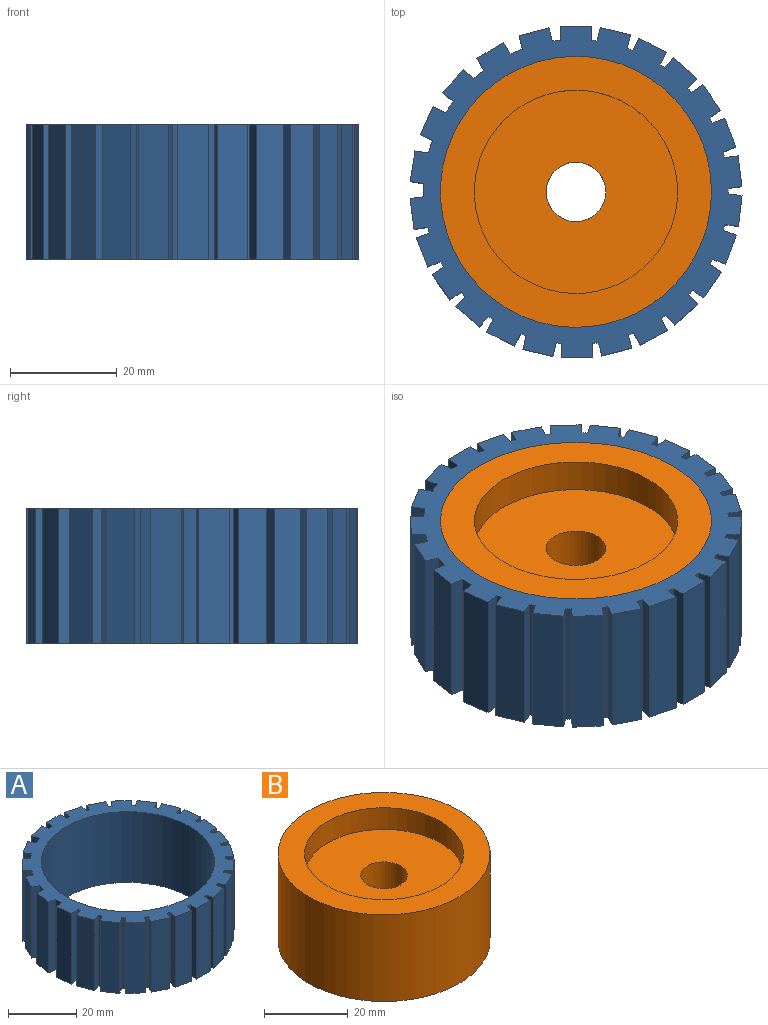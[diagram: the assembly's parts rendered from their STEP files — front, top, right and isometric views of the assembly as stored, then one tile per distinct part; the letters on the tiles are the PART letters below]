
ASSEMBLY  parts=2 mates=1
PART A: 103 faces, bbox 62.2x62x25.4 mm
  f0: plane 25.4x2.54mm, normal (0.13,-0.99,0), area 65.2mm2, adj f1,f99,f101,f102
  f1: cylinder r=28.57mm len=25.4mm, axis (0,0,-1), area 27.2mm2, adj f0,f2,f101,f102
  f2: plane 25.4x2.39mm, normal (-0.37,0.93,0), area 65.2mm2, adj f1,f3,f101,f102
  f3: plane 25.4x5.4mm, normal (-0.93,-0.37,0), area 147.4mm2, adj f2,f4,f101,f102
  f4: plane 25.4x2.39mm, normal (0.37,-0.93,0), area 65.2mm2, adj f3,f5,f101,f102
  f5: cylinder r=28.57mm len=25.4mm, axis (0,0,-1), area 27.2mm2, adj f4,f6,f101,f102
  f6: plane 25.4x2.09mm, normal (-0.58,0.82,0), area 65.2mm2, adj f5,f7,f101,f102
  f7: plane 25.4x4.74mm, normal (-0.82,-0.58,0), area 147.4mm2, adj f6,f8,f101,f102
  f8: plane 25.4x2.09mm, normal (0.58,-0.82,0), area 65.2mm2, adj f7,f9,f101,f102
  f9: cylinder r=28.57mm len=25.4mm, axis (0,0,-1), area 27.2mm2, adj f8,f10,f101,f102
  f10: plane 25.4x1.94mm, normal (-0.76,0.65,0), area 65.2mm2, adj f9,f11,f101,f102
  f11: plane 25.4x4.39mm, normal (-0.65,-0.76,0), area 147.4mm2, adj f10,f12,f101,f102
  f12: plane 25.4x1.94mm, normal (0.76,-0.65,0), area 65.2mm2, adj f11,f13,f101,f102
  f13: cylinder r=28.57mm len=25.4mm, axis (0,0,-1), area 27.2mm2, adj f12,f14,f101,f102
  f14: plane 25.4x2.28mm, normal (-0.89,0.46,0), area 65.2mm2, adj f13,f15,f101,f102
  f15: plane 25.4x5.17mm, normal (-0.46,-0.89,0), area 147.4mm2, adj f14,f16,f101,f102
  f16: plane 25.4x2.28mm, normal (0.89,-0.46,0), area 65.2mm2, adj f15,f17,f101,f102
  f17: cylinder r=28.57mm len=25.4mm, axis (0,0,-1), area 27.2mm2, adj f16,f18,f101,f102
  f18: plane 25.4x2.5mm, normal (-0.97,0.23,0), area 65.2mm2, adj f17,f19,f101,f102
  f19: plane 25.4x5.65mm, normal (-0.23,-0.97,0), area 147.4mm2, adj f18,f20,f101,f102
  f20: plane 25.4x2.5mm, normal (0.97,-0.23,0), area 65.2mm2, adj f19,f21,f101,f102
  f21: cylinder r=28.57mm len=25.4mm, axis (0,0,-1), area 27.2mm2, adj f20,f22,f101,f102
  f22: plane 25.4x2.57mm, normal (-1,-0.01,0), area 65.2mm2, adj f21,f23,f101,f102
  f23: plane 25.4x5.8mm, normal (0.01,-1,0), area 147.4mm2, adj f22,f24,f101,f102
  f24: plane 25.4x2.57mm, normal (1,0.01,0), area 65.2mm2, adj f23,f25,f101,f102
  f25: cylinder r=28.57mm len=25.4mm, axis (0,0,-1), area 27.2mm2, adj f24,f26,f101,f102
  f26: plane 25.4x2.49mm, normal (-0.97,-0.25,0), area 65.2mm2, adj f25,f27,f101,f102
  f27: plane 25.4x5.62mm, normal (0.25,-0.97,0), area 147.4mm2, adj f26,f28,f101,f102
  f28: plane 25.4x2.49mm, normal (0.97,0.25,0), area 65.2mm2, adj f27,f29,f101,f102
  f29: cylinder r=28.57mm len=25.4mm, axis (0,0,-1), area 27.2mm2, adj f28,f30,f101,f102
  f30: plane 25.4x2.26mm, normal (-0.88,-0.47,0), area 65.2mm2, adj f29,f31,f101,f102
  f31: plane 25.4x5.12mm, normal (0.47,-0.88,0), area 147.4mm2, adj f30,f32,f101,f102
  f32: plane 25.4x2.26mm, normal (0.88,0.47,0), area 65.2mm2, adj f31,f33,f101,f102
  f33: cylinder r=28.57mm len=25.4mm, axis (0,0,-1), area 27.2mm2, adj f32,f34,f101,f102
  f34: plane 25.4x1.91mm, normal (-0.74,-0.67,0), area 65.2mm2, adj f33,f35,f101,f102
  f35: plane 25.4x4.32mm, normal (0.67,-0.74,0), area 147.4mm2, adj f34,f36,f101,f102
  f36: plane 25.4x1.91mm, normal (0.74,0.67,0), area 65.2mm2, adj f35,f37,f101,f102
  f37: cylinder r=28.57mm len=25.4mm, axis (0,0,-1), area 27.2mm2, adj f36,f38,f101,f102
  f38: plane 25.4x2.12mm, normal (-0.56,-0.83,0), area 65.2mm2, adj f37,f39,f101,f102
  f39: plane 25.4x4.8mm, normal (0.83,-0.56,0), area 147.4mm2, adj f38,f40,f101,f102
  f40: plane 25.4x2.12mm, normal (0.56,0.83,0), area 65.2mm2, adj f39,f41,f101,f102
  f41: cylinder r=28.57mm len=25.4mm, axis (0,0,-1), area 27.2mm2, adj f40,f42,f101,f102
  f42: plane 25.4x2.4mm, normal (-0.35,-0.94,0), area 65.2mm2, adj f41,f43,f101,f102
  f43: plane 25.4x5.44mm, normal (0.94,-0.35,0), area 147.4mm2, adj f42,f44,f101,f102
  f44: plane 25.4x2.4mm, normal (0.35,0.94,0), area 65.2mm2, adj f43,f45,f101,f102
  f45: cylinder r=28.57mm len=25.4mm, axis (0,0,-1), area 27.2mm2, adj f44,f46,f101,f102
  f46: plane 25.4x2.55mm, normal (-0.12,-0.99,0), area 65.2mm2, adj f45,f47,f101,f102
  f47: plane 25.4x5.76mm, normal (0.99,-0.12,0), area 147.4mm2, adj f46,f48,f101,f102
  f48: plane 25.4x2.55mm, normal (0.12,0.99,0), area 65.2mm2, adj f47,f49,f101,f102
  f49: cylinder r=28.57mm len=25.4mm, axis (0,0,-1), area 27.2mm2, adj f48,f50,f101,f102
  f50: plane 25.4x2.55mm, normal (0.12,-0.99,0), area 65.2mm2, adj f49,f51,f101,f102
  f51: plane 25.4x5.76mm, normal (0.99,0.12,0), area 147.4mm2, adj f50,f52,f101,f102
  f52: plane 25.4x2.55mm, normal (-0.12,0.99,0), area 65.2mm2, adj f51,f53,f101,f102
  f53: cylinder r=28.57mm len=25.4mm, axis (0,0,-1), area 27.2mm2, adj f52,f54,f101,f102
  f54: plane 25.4x2.4mm, normal (0.36,-0.93,0), area 65.2mm2, adj f53,f55,f101,f102
  f55: plane 25.4x5.42mm, normal (0.93,0.36,0), area 147.4mm2, adj f54,f56,f101,f102
  f56: plane 25.4x2.4mm, normal (-0.36,0.93,0), area 65.2mm2, adj f55,f57,f101,f102
  f57: cylinder r=28.57mm len=25.4mm, axis (0,0,-1), area 27.2mm2, adj f56,f58,f101,f102
  f58: plane 25.4x2.11mm, normal (0.57,-0.82,0), area 65.2mm2, adj f57,f59,f101,f102
  f59: plane 25.4x4.77mm, normal (0.82,0.57,0), area 147.4mm2, adj f58,f60,f101,f102
  f60: plane 25.4x2.11mm, normal (-0.57,0.82,0), area 65.2mm2, adj f59,f61,f101,f102
  f61: cylinder r=28.57mm len=25.4mm, axis (0,0,-1), area 27.2mm2, adj f60,f62,f101,f102
  f62: plane 25.4x1.92mm, normal (0.75,-0.66,0), area 65.2mm2, adj f61,f63,f101,f102
  f63: plane 25.4x4.35mm, normal (0.66,0.75,0), area 147.4mm2, adj f62,f64,f101,f102
  f64: plane 25.4x1.92mm, normal (-0.75,0.66,0), area 65.2mm2, adj f63,f65,f101,f102
  f65: cylinder r=28.57mm len=25.4mm, axis (0,0,-1), area 27.2mm2, adj f64,f66,f101,f102
  f66: plane 25.4x2.27mm, normal (0.89,-0.46,0), area 65.2mm2, adj f65,f67,f101,f102
  f67: plane 25.4x5.14mm, normal (0.46,0.89,0), area 147.4mm2, adj f66,f68,f101,f102
  f68: plane 25.4x2.27mm, normal (-0.89,0.46,0), area 65.2mm2, adj f67,f69,f101,f102
  f69: cylinder r=28.57mm len=25.4mm, axis (0,0,-1), area 27.2mm2, adj f68,f70,f101,f102
  f70: plane 25.4x2.49mm, normal (0.97,-0.24,0), area 65.2mm2, adj f69,f71,f101,f102
  f71: plane 25.4x5.64mm, normal (0.24,0.97,0), area 147.4mm2, adj f70,f72,f101,f102
  f72: plane 25.4x2.49mm, normal (-0.97,0.24,0), area 65.2mm2, adj f71,f73,f101,f102
  f73: cylinder r=28.57mm len=25.4mm, axis (0,0,-1), area 27.2mm2, adj f72,f74,f101,f102
  f74: plane 25.4x2.57mm, normal (1,0,0), area 65.2mm2, adj f73,f75,f101,f102
  f75: plane 25.4x5.8mm, normal (0,1,0), area 147.4mm2, adj f74,f76,f101,f102
  f76: plane 25.4x2.57mm, normal (-1,0,0), area 65.2mm2, adj f75,f77,f101,f102
  f77: cylinder r=28.57mm len=25.4mm, axis (0,0,-1), area 38.6mm2, adj f76,f78,f101,f102
  f78: plane 25.4x2.48mm, normal (0.97,0.25,0), area 65.2mm2, adj f77,f79,f101,f102
  f79: plane 25.4x5.61mm, normal (-0.25,0.97,0), area 147.4mm2, adj f78,f80,f101,f102
  f80: plane 25.4x2.48mm, normal (-0.97,-0.25,0), area 65.2mm2, adj f79,f81,f101,f102
  f81: cylinder r=28.57mm len=25.4mm, axis (0,0,-1), area 62.6mm2, adj f80,f82,f101,f102
  f82: plane 25.4x2.19mm, normal (0.85,0.52,0), area 65.2mm2, adj f81,f83,f101,f102
  f83: plane 25.4x4.96mm, normal (-0.52,0.85,0), area 147.4mm2, adj f82,f84,f101,f102
  f84: plane 25.4x2.19mm, normal (-0.85,-0.52,0), area 65.2mm2, adj f83,f85,f101,f102
  f85: cylinder r=28.57mm len=25.4mm, axis (0,0,-1), area 62.6mm2, adj f84,f86,f101,f102
  f86: plane 25.4x1.9mm, normal (0.67,0.74,0), area 65.2mm2, adj f85,f87,f101,f102
  f87: plane 25.4x4.31mm, normal (-0.74,0.67,0), area 147.4mm2, adj f86,f88,f101,f102
  f88: plane 25.4x1.9mm, normal (-0.67,-0.74,0), area 65.2mm2, adj f87,f89,f101,f102
  f89: cylinder r=28.57mm len=25.4mm, axis (0,0,-1), area 62.6mm2, adj f88,f90,f101,f102
  f90: plane 25.4x2.32mm, normal (0.43,0.9,0), area 65.2mm2, adj f89,f91,f101,f102
  f91: plane 25.4x5.24mm, normal (-0.9,0.43,0), area 147.4mm2, adj f90,f92,f101,f102
  f92: plane 25.4x2.32mm, normal (-0.43,-0.9,0), area 65.2mm2, adj f91,f93,f101,f102
  f93: cylinder r=28.57mm len=25.4mm, axis (0,0,-1), area 62.6mm2, adj f92,f94,f101,f102
  f94: plane 25.4x2.53mm, normal (0.16,0.99,0), area 65.2mm2, adj f93,f95,f101,f102
  f95: plane 25.4x5.73mm, normal (-0.99,0.16,0), area 147.4mm2, adj f94,f96,f101,f102
  f96: plane 25.4x2.53mm, normal (-0.16,-0.99,0), area 65.2mm2, adj f95,f97,f101,f102
  f97: cylinder r=28.57mm len=25.4mm, axis (0,0,-1), area 62.6mm2, adj f96,f98,f101,f102
  f98: plane 25.4x2.54mm, normal (-0.13,0.99,0), area 65.2mm2, adj f97,f99,f101,f102
  f99: plane 25.4x5.75mm, normal (-0.99,-0.13,0), area 147.4mm2, adj f0,f98,f101,f102
  f100: cylinder r=25.4mm len=50.8mm, axis (0,0,-1), area 4053.7mm2, adj f101,f102
  f101: plane 62.22x62.01mm, normal (0,0,1), area 896.3mm2, adj f0,f1,f2,f3,f4,f5,f6,f7
  f102: plane 62.22x62.01mm, normal (0,0,-1), area 896.3mm2, adj f0,f1,f2,f3,f4,f5,f6,f7
PART B: 8 faces, bbox 50.8x50.8x25.4 mm
  f0: cylinder r=25.4mm len=50.8mm, axis (0,0,-1), area 4053.7mm2, adj f1,f2
  f1: plane 50.8x50.8mm, normal (0,0,1), area 886.7mm2, adj f0,f3
  f2: plane 50.8x50.8mm, normal (0,0,-1), area 886.7mm2, adj f0,f5
  f3: cylinder r=19.05mm len=38.1mm, axis (0,0,1), area 760.1mm2, adj f1,f4
  f4: plane 38.1x38.1mm, normal (0,0,1), area 1042.3mm2, adj f3,f7
  f5: cylinder r=19.05mm len=38.1mm, axis (0,0,-1), area 760.1mm2, adj f2,f6
  f6: plane 38.1x38.1mm, normal (0,0,-1), area 1042.3mm2, adj f5,f7
  f7: cylinder r=5.58mm len=12.7mm, axis (0,0,1), area 445.2mm2, adj f4,f6
PLACE A t=(16.1,-21.64,13.64)mm
PLACE B t=(16.1,-21.64,13.64)mm
MATE fastened A.f100 <-> B.f0  axis (0,0,-1) through (16.1,-21.64,26.34)mm
